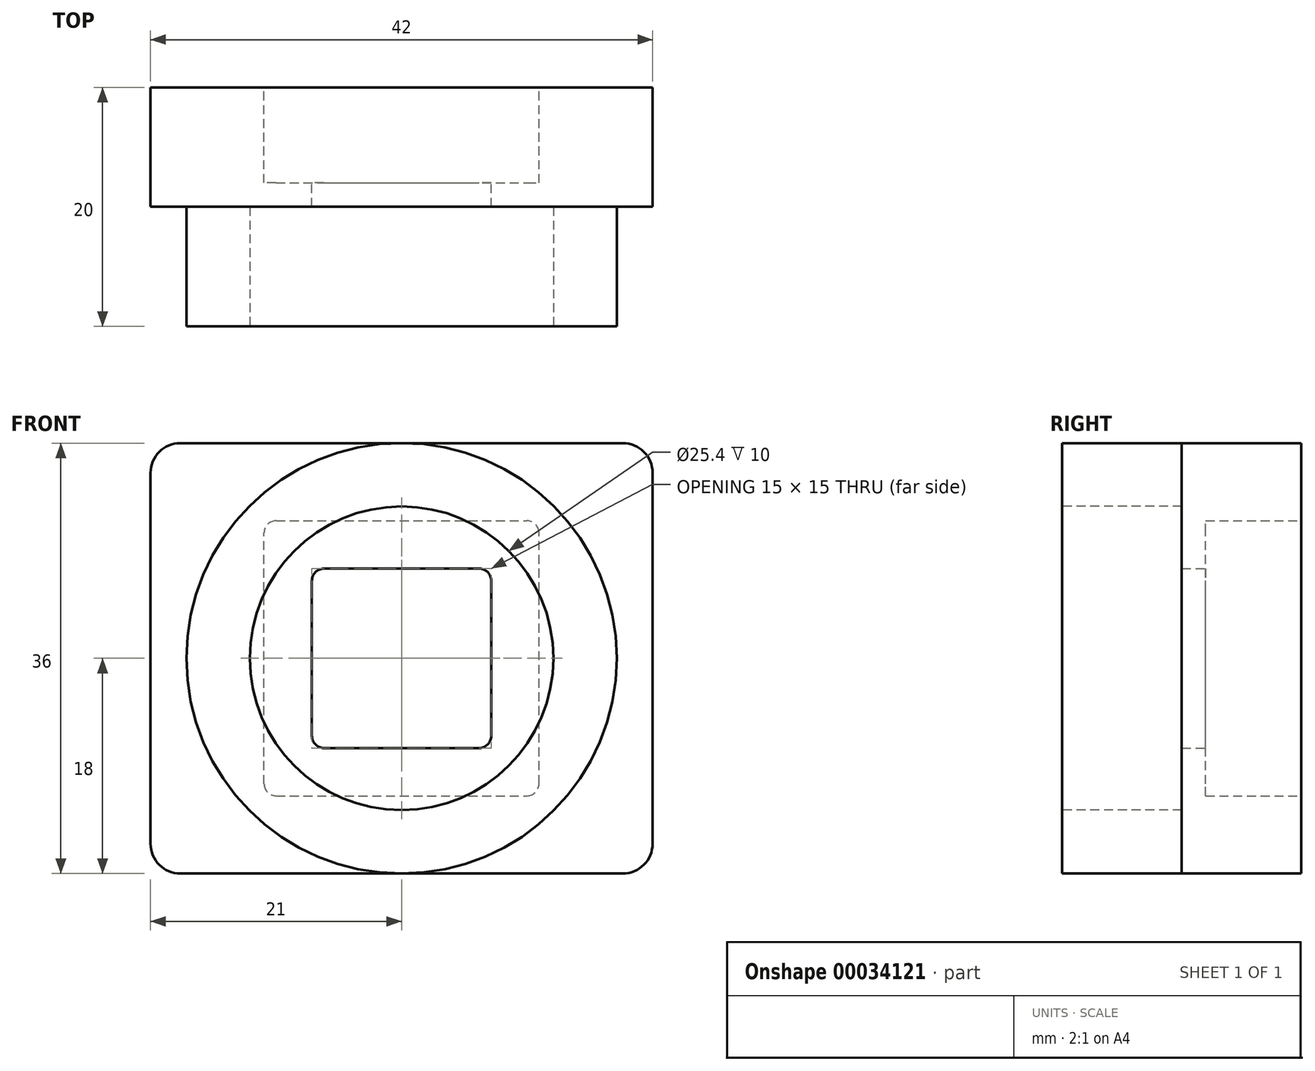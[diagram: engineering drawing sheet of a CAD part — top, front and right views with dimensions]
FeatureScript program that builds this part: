
annotation { "Feature Type Name" : "Feature", "Feature Type Description" : "" }
export const myFeature = defineFeature(function(context is Context, id is Id, definition is map)
    precondition{}
    {
        {
            var Q0;
            Q0=qCreatedBy(makeId("Front.planeOp"),FACE);
            var sketch = newSketch(context, id + "F0", { "sketchPlane" : qUnion([Q0])});
            skLineSegment(sketch, "E0.rect.bottom", {"start": v(21, -18) * mm, "end": v(-21, -18) * mm});
            skLineSegment(sketch, "E0.rect.top", {"start": v(21, 18) * mm, "end": v(-21, 18) * mm});
            skLineSegment(sketch, "E0.rect.left", {"start": v(21, -18) * mm, "end": v(21, 18) * mm});
            skLineSegment(sketch, "E0.rect.right", {"start": v(-21, -18) * mm, "end": v(-21, 18) * mm});
            skPoint(sketch, "E0.rect.middle", {"position": v(0, 0) * mm});
            skSolve(sketch);
        }
        {
            var Q0;
            Q0 = qSketchRegion(id + "F0", true);
            extrude(context, id + "F1", {"entities" : qUnion([Q0]), "oppositeDirection" : true, "depth" : 10 * mm});
        }
        {
            var Q0;
            Q0=qCreatedBy(makeId("Front.planeOp"),FACE);
            var sketch = newSketch(context, id + "F2", { "sketchPlane" : qUnion([Q0])});
            skCircle(sketch, "E1", {"center": v(0, 0) * mm, "radius": 18 * mm});
            skSolve(sketch);
        }
        {
            var Q0;
            Q0 = qSketchRegion(id + "F2", true);
            extrude(context, id + "F3", {"entities" : qUnion([Q0]), "operationType" : NewBodyOperationType.ADD, "depth" : 10 * mm});
        }
        {
            var Q0;
            Q0=makeQuery(id+"F3.opExtrude","CAP_FACE",FACE,{"disambiguationData":[OSD([sQuery(id+"F2.wireOp",EDGE,"E1")])],"isStart":false});
            var sketch = newSketch(context, id + "F4", { "sketchPlane" : qUnion([Q0])});
            skCircle(sketch, "E2", {"center": v(0, 0) * mm, "radius": 12.7 * mm});
            skSolve(sketch);
        }
        {
            var Q0;
            Q0 = qSketchRegion(id + "F4", true);
            extrude(context, id + "F5", {"entities" : qUnion([Q0]), "operationType" : NewBodyOperationType.REMOVE, "oppositeDirection" : true, "depth" : 10 * mm});
        }
        {
            var Q0;
            Q0=makeQuery(id+"F1.opExtrude","CAP_FACE",FACE,{"disambiguationData":[OSD([sQuery(id+"F0.wireOp",EDGE,"E0.rect.bottom"),sQuery(id+"F0.wireOp",EDGE,"E0.rect.top"),sQuery(id+"F0.wireOp",EDGE,"E0.rect.left"),sQuery(id+"F0.wireOp",EDGE,"E0.rect.right")])],"isStart":false});
            var sketch = newSketch(context, id + "F6", { "sketchPlane" : qUnion([Q0])});
            skLineSegment(sketch, "E3.rect.bottom", {"start": v(11.5, -11.5) * mm, "end": v(-11.5, -11.5) * mm});
            skLineSegment(sketch, "E3.rect.top", {"start": v(11.5, 11.5) * mm, "end": v(-11.5, 11.5) * mm});
            skLineSegment(sketch, "E3.rect.left", {"start": v(11.5, -11.5) * mm, "end": v(11.5, 11.5) * mm});
            skLineSegment(sketch, "E3.rect.right", {"start": v(-11.5, -11.5) * mm, "end": v(-11.5, 11.5) * mm});
            skPoint(sketch, "E3.rect.middle", {"position": v(0, 0) * mm});
            skSolve(sketch);
        }
        {
            var Q0;
            Q0 = qSketchRegion(id + "F6", true);
            extrude(context, id + "F7", {"entities" : qUnion([Q0]), "operationType" : NewBodyOperationType.REMOVE, "oppositeDirection" : true, "depth" : 8 * mm});
        }
        {
            var Q0;
            Q0=makeQuery(id+"F7.boolean.opBoolean","COPY",FACE,{"derivedFrom":makeQuery(id+"F7.opExtrude","CAP_FACE",FACE,{"disambiguationData":[OSD([sQuery(id+"F6.wireOp",EDGE,"E3.rect.bottom"),sQuery(id+"F6.wireOp",EDGE,"E3.rect.top"),sQuery(id+"F6.wireOp",EDGE,"E3.rect.left"),sQuery(id+"F6.wireOp",EDGE,"E3.rect.right")])],"isStart":false})});
            var sketch = newSketch(context, id + "F8", { "sketchPlane" : qUnion([Q0])});
            skLineSegment(sketch, "E4.rect.bottom", {"start": v(7.5, -7.5) * mm, "end": v(-7.5, -7.5) * mm});
            skLineSegment(sketch, "E4.rect.top", {"start": v(7.5, 7.5) * mm, "end": v(-7.5, 7.5) * mm});
            skLineSegment(sketch, "E4.rect.left", {"start": v(7.5, -7.5) * mm, "end": v(7.5, 7.5) * mm});
            skLineSegment(sketch, "E4.rect.right", {"start": v(-7.5, -7.5) * mm, "end": v(-7.5, 7.5) * mm});
            skPoint(sketch, "E4.rect.middle", {"position": v(0, 0) * mm});
            skSolve(sketch);
        }
        {
            var Q0;
            Q0 = qSketchRegion(id + "F8", true);
            extrude(context, id + "F9", {"entities" : qUnion([Q0]), "operationType" : NewBodyOperationType.REMOVE, "endBound" : BoundingType.THROUGH_ALL, "oppositeDirection" : true, "depth" : 25 * mm});
        }
        {
            var Q0;
            Q0=makeQuery(id+"F7.boolean.opBoolean","COPY",EDGE,{"derivedFrom":makeQuery(id+"F7.opExtrude","SWEPT_EDGE",EDGE,{"disambiguationData":[OSD([sQuery(id+"F6.wireOp",EDGE,"E3.rect.top"),sQuery(id+"F6.wireOp",EDGE,"E3.rect.right")])]})});
            var Q1;
            Q1=makeQuery(id+"F7.boolean.opBoolean","COPY",EDGE,{"derivedFrom":makeQuery(id+"F7.opExtrude","SWEPT_EDGE",EDGE,{"disambiguationData":[OSD([sQuery(id+"F6.wireOp",EDGE,"E3.rect.top"),sQuery(id+"F6.wireOp",EDGE,"E3.rect.left")])]})});
            var Q2;
            Q2=makeQuery(id+"F7.boolean.opBoolean","COPY",EDGE,{"derivedFrom":makeQuery(id+"F7.opExtrude","SWEPT_EDGE",EDGE,{"disambiguationData":[OSD([sQuery(id+"F6.wireOp",EDGE,"E3.rect.bottom"),sQuery(id+"F6.wireOp",EDGE,"E3.rect.right")])]})});
            var Q3;
            Q3=makeQuery(id+"F7.boolean.opBoolean","COPY",EDGE,{"derivedFrom":makeQuery(id+"F7.opExtrude","SWEPT_EDGE",EDGE,{"disambiguationData":[OSD([sQuery(id+"F6.wireOp",EDGE,"E3.rect.bottom"),sQuery(id+"F6.wireOp",EDGE,"E3.rect.left")])]})});
            var Q4;
            Q4=makeQuery(id+"F9.boolean.opBoolean","COPY",EDGE,{"derivedFrom":makeQuery(id+"F9.opExtrude","SWEPT_EDGE",EDGE,{"disambiguationData":[OSD([sQuery(id+"F8.wireOp",EDGE,"E4.rect.bottom"),sQuery(id+"F8.wireOp",EDGE,"E4.rect.left")])]})});
            var Q5;
            Q5=makeQuery(id+"F9.boolean.opBoolean","COPY",EDGE,{"derivedFrom":makeQuery(id+"F9.opExtrude","SWEPT_EDGE",EDGE,{"disambiguationData":[OSD([sQuery(id+"F8.wireOp",EDGE,"E4.rect.bottom"),sQuery(id+"F8.wireOp",EDGE,"E4.rect.right")])]})});
            var Q6;
            Q6=makeQuery(id+"F9.boolean.opBoolean","COPY",EDGE,{"derivedFrom":makeQuery(id+"F9.opExtrude","SWEPT_EDGE",EDGE,{"disambiguationData":[OSD([sQuery(id+"F8.wireOp",EDGE,"E4.rect.top"),sQuery(id+"F8.wireOp",EDGE,"E4.rect.right")])]})});
            var Q7;
            Q7=makeQuery(id+"F9.boolean.opBoolean","COPY",EDGE,{"derivedFrom":makeQuery(id+"F9.opExtrude","SWEPT_EDGE",EDGE,{"disambiguationData":[OSD([sQuery(id+"F8.wireOp",EDGE,"E4.rect.top"),sQuery(id+"F8.wireOp",EDGE,"E4.rect.left")])]})});
            fillet(context, id + "F10", {"entities" : qUnion([Q0, Q1, Q2, Q3, Q4, Q5, Q6, Q7]), "radius" : 1 * mm, "tangentPropagation" : true, "allowEdgeOverflow" : false});
        }
        {
            var Q0;
            Q0=makeQuery(id+"F1.opExtrude","SWEPT_EDGE",EDGE,{"disambiguationData":[OSD([sQuery(id+"F0.wireOp",EDGE,"E0.rect.top"),sQuery(id+"F0.wireOp",EDGE,"E0.rect.right")])]});
            var Q1;
            Q1=makeQuery(id+"F1.opExtrude","SWEPT_EDGE",EDGE,{"disambiguationData":[OSD([sQuery(id+"F0.wireOp",EDGE,"E0.rect.bottom"),sQuery(id+"F0.wireOp",EDGE,"E0.rect.right")])]});
            var Q2;
            Q2=makeQuery(id+"F1.opExtrude","SWEPT_EDGE",EDGE,{"disambiguationData":[OSD([sQuery(id+"F0.wireOp",EDGE,"E0.rect.top"),sQuery(id+"F0.wireOp",EDGE,"E0.rect.left")])]});
            var Q3;
            Q3=makeQuery(id+"F1.opExtrude","SWEPT_EDGE",EDGE,{"disambiguationData":[OSD([sQuery(id+"F0.wireOp",EDGE,"E0.rect.bottom"),sQuery(id+"F0.wireOp",EDGE,"E0.rect.left")])]});
            fillet(context, id + "F11", {"entities" : qUnion([Q0, Q1, Q2, Q3]), "radius" : 2.5 * mm, "tangentPropagation" : true, "allowEdgeOverflow" : false});
        }
    });
